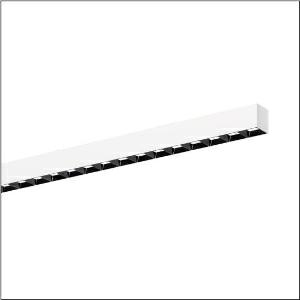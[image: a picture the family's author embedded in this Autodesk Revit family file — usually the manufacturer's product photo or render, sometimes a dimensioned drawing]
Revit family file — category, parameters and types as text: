
# Revit family: silica_r__21_51mx24tat4w_113b
name_source: partatom
category: Lighting Fixtures
units: mm (PartAtom-declared; Revit-internal decimal feet)

## family parameters
Cut with Voids When Loaded = No
Host = Face
Light Source = No
Part Type = Normal
Room Calculation Point = No
Round Connector Dimension = Use Diameter
Shared = No

## types (1)
- --- (1 x LED, 3280 lm, 32.4 W, 6500K)
    Apparent Load = 32 VA
    CIE Flux Codes = 74 94 99 100 100
    Color Rendering = 80
    Color Temperature = 6500K
    Default Elevation = 1800 mm
    Description = Silica® 21, office luminaire, primary light control with darklight reflector, of PMMA, black, light emission: direct distribution, primary light characteristic: asymmetric, installation type: surface-mounted, LED, rated luminous flux: 3.280lm, luminous efficacy: 96lm/W, light colour: 8tw, colour temperature: 2700..6500K, control gear: ECG DALI, with terminal, 3+2-pole, max. 2.5mm², mains connection: 220..240V, AC, 50/60Hz, rated input power: 34.1W, luminaire housing, of aluminium, traffic white (RAL 9016), length: 1.204mm, width: 53mm, height: 53mm, protection rating (complete): IP20, insulation class (complete): insulation class I (protective earthing), certification: CE, permissible operating ambient temperature: 0..+35°C, standard: EN 50419, packaging unit: 1 piece
    Height = 0 mm  [stored 0 ft]
    Lamp = 1 x LED
    Lamp Light Flux = 3280 lm
    Lamp Power = 32.4 W
    Lamp count = 1
    Length = 1204 mm
    Luminous efficacy = 101 lm/W
    Manufacturer = Siteco
    ModVariant = No
    Model = 51MX24TAT4W
    Mounting Place = Ceiling
    Mounting Type = Recessed
    Number of Poles = 1
    OnlyDefault = Yes
    Power Factor = 1
    Product Name = Silica® 21
    Product group = office luminaire | ceiling recessed
    ProductGroupID = 400
    Protection Class = Protection class I
    Protection Degree = IP 20
    RLX_Detail_Level = 1
    RLX_Emergency_Light_Flux = 0 lm
    RLX_Emergency_Type = 0
    RLX_Emergency_Type_DB = No
    RlxData = <blob elided: 38289 chars, md5=8a146549>
    Socket = socket
    Standby Power = 0 W
    System Light Flux = 3280 lm
    System Power = 32 W
    Type Comments = individual setting
    Type Image = l_1335873.jpg
    URL = http://relux.com
    VarID = @adj_109819
    Voltage = 0 V
    Weight = 0.00 kg
    Width = 53 mm

note: [stored X ft] marks values corroborated as IEEE doubles in the binary element streams (Revit-internal decimal feet)

## geometry (parser evidence)
native form markers: Blend x4, Sweep x13
no freeform markers — native parametric forms only
